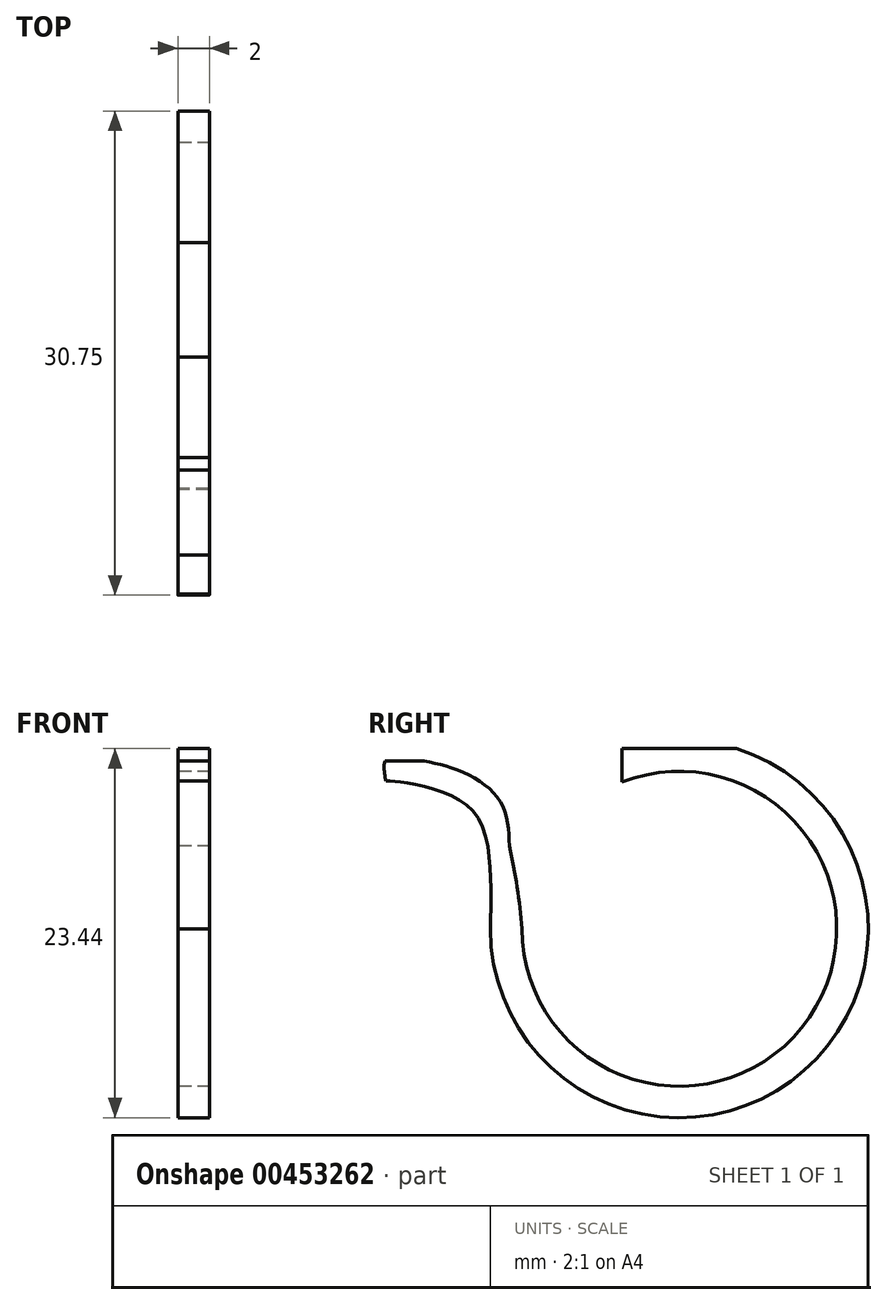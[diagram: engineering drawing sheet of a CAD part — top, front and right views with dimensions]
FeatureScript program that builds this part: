
annotation { "Feature Type Name" : "Feature", "Feature Type Description" : "" }
export const myFeature = defineFeature(function(context is Context, id is Id, definition is map)
    precondition{}
    {
        {
            var Q0;
            Q0=qCreatedBy(makeId("Right.planeOp"),FACE);
            var sketch = newSketch(context, id + "F0", { "sketchPlane" : qUnion([Q0])});
            skArc(sketch, "E0", {"start": v(-10, 0) * mm, "mid": v(8.26, -5.64) * mm, "end": v(-3.64, 9.31) * mm});
            skPoint(sketch, "E1.start.orphan", {"position": v(-12, 0) * mm});
            skPoint(sketch, "E2.start.orphan", {"position": v(-12, 10.17) * mm});
            skFitSpline(sketch, "E3", {"points": [v(-12, 0) * mm, v(-12, 3.62) * mm, v(-12.87, 7.18) * mm, v(-15.33, 8.78) * mm, v(-17.78, 9.33) * mm, v(-18.64, 9.4) * mm], "startDerivative": vector(0.43, 14.9) * mm, "endDerivative": vector(-6.49, 0.22) * mm});
            skFitSpline(sketch, "E4", {"points": [v(-10.8, 5.25) * mm, v(-11.09, 7.49) * mm, v(-12.44, 9.2) * mm, v(-14.77, 10.31) * mm, v(-16.92, 10.8) * mm, v(-18.58, 10.8) * mm, v(-18.64, 9.4) * mm], "startDerivative": vector(-0.41, 13.27) * mm, "endDerivative": vector(2.2, -12.62) * mm});
            skPoint(sketch, "E5.start.orphan", {"position": v(-12, 12.4) * mm});
            skLineSegment(sketch, "E6", {"start": v(-3.64, 11.44) * mm, "end": v(3.64, 11.44) * mm});
            skLineSegment(sketch, "E7", {"start": v(-18.68, 10.67) * mm, "end": v(-16.2, 10.67) * mm});
            skArc(sketch, "E8.trimOffspring", {"start": v(-11.98, 0.67) * mm, "mid": v(6.8, -9.88) * mm, "end": v(3.64, 11.44) * mm});
            skArc(sketch, "E9", {"start": v(-10, 0) * mm, "mid": v(-10.3, 2.64) * mm, "end": v(-10.8, 5.25) * mm});
            skLineSegment(sketch, "E10", {"start": v(-3.64, 11.44) * mm, "end": v(-3.64, 9.31) * mm});
            skSolve(sketch);
        }
        {
            var Q0;
            Q0=makeQuery(id+"F0.imprint","IMPRINT",FACE,{"disambiguationData":[TD([[makeQuery(id+"F0.imprint","IMPRINT",EDGE,{"derivedFrom":sQuery(id+"F0.wireOp",EDGE,"E0")}),-1.0]])]});
            extrude(context, id + "F1", {"entities" : qUnion([Q0]), "depth" : 2 * mm});
        }
    });
